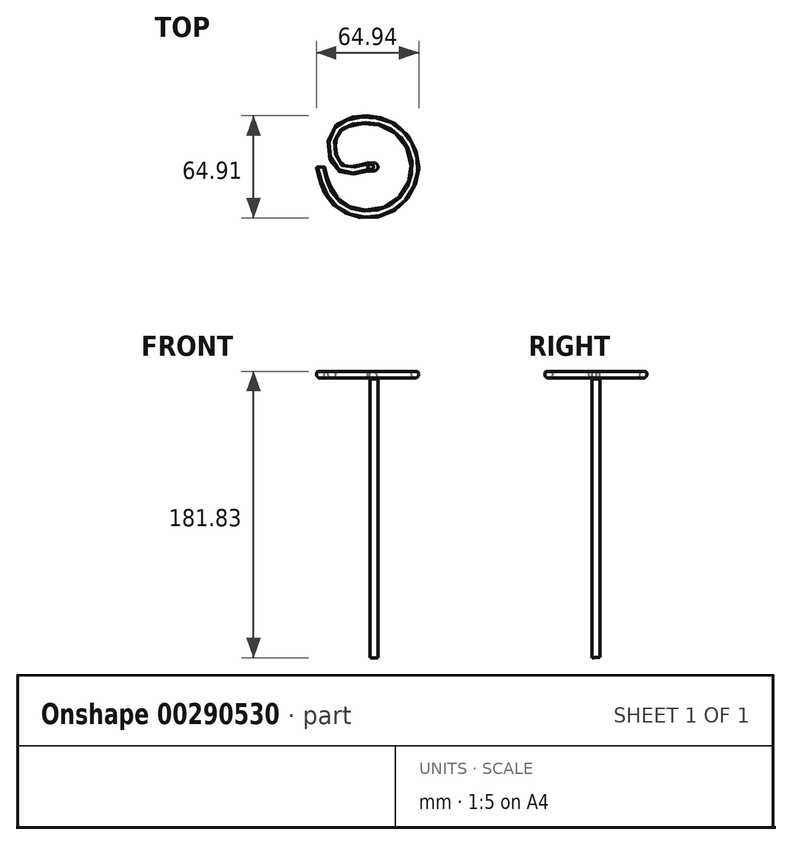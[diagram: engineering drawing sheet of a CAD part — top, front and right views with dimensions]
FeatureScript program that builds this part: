
annotation { "Feature Type Name" : "Feature", "Feature Type Description" : "" }
export const myFeature = defineFeature(function(context is Context, id is Id, definition is map)
    precondition{}
    {
        {
            var Q0;
            Q0=qCreatedBy(makeId("Top.planeOp"),FACE);
            var sketch = newSketch(context, id + "F0", { "sketchPlane" : qUnion([Q0])});
            skArc(sketch, "E0", {"start": v(-21.21, -21.21) * mm, "mid": v(27.72, -11.48) * mm, "end": v(0, 30) * mm});
            skFitSpline(sketch, "E1", {"points": [v(-30, 0) * mm, v(-21.21, -21.21) * mm, v(0, -30) * mm, v(21.21, -21.21) * mm, v(30, 0) * mm, v(21.21, 21.21) * mm, v(0, 30) * mm, v(-21.21, 21.21) * mm, v(-17.95, 0) * mm, v(0, 0) * mm], "startDerivative": vector(49.75, -208.07) * mm, "endDerivative": vector(203.75, 55.38) * mm});
            skSolve(sketch);
        }
        {
            var Q0;
            Q0=qCreatedBy(makeId("Front.planeOp"),FACE);
            var sketch = newSketch(context, id + "F1", { "sketchPlane" : qUnion([Q0])});
            skCircle(sketch, "E2", {"center": v(-30, 0) * mm, "radius": 2.5 * mm});
            skSolve(sketch);
        }
        {
            var Q0;
            Q0=makeQuery(id+"F1.imprint","IMPRINT",FACE,{"disambiguationData":[TD([[makeQuery(id+"F1.imprint","IMPRINT",EDGE,{"derivedFrom":sQuery(id+"F1.wireOp",EDGE,"E2")}),1.0]])]});
            var Q1;
            Q1=sQuery(id+"F0.wireOp",EDGE,"E1");
            sweep(context, id + "F2", {"profiles" : qUnion([Q0]), "path" : qUnion([Q1])});
        }
        {
            var Q0;
            Q0=qCreatedBy(makeId("Front.planeOp"),FACE);
            var sketch = newSketch(context, id + "F3", { "sketchPlane" : qUnion([Q0])});
            skLineSegment(sketch, "E3", {"start": v(0, 0) * mm, "end": v(1, 0) * mm});
            skLineSegment(sketch, "E4", {"start": v(4, -3) * mm, "end": v(4, -180) * mm});
            skPoint(sketch, "E5.visualSharp", {"position": v(4, 0) * mm});
            skArc(sketch, "E5.filletArc", {"start": v(4, -3) * mm, "mid": v(3.12, -0.88) * mm, "end": v(1, 0) * mm});
            skSolve(sketch);
        }
        {
            var Q0;
            Q0=makeQuery(id+"F2.opSweep","CAP_FACE",FACE,{"disambiguationData":[OSD([sQuery(id+"F0.wireOp",VERTEX,"E1.end"),sQuery(id+"F1.wireOp",EDGE,"E2")])],"isStart":false});
            var Q1;
            Q1=sQuery(id+"F3.wireOp",EDGE,"E3");
            var Q2;
            Q2=sQuery(id+"F3.wireOp",EDGE,"E5.filletArc");
            var Q3;
            Q3=sQuery(id+"F3.wireOp",EDGE,"E4");
            sweep(context, id + "F4", {"profiles" : qUnion([Q0]), "path" : qUnion([Q1, Q2, Q3])});
        }
        {
            var Q0;
            Q0=qCreatedBy(makeId("Right.planeOp"),FACE);
            var sketch = newSketch(context, id + "F5", { "sketchPlane" : qUnion([Q0])});
            skLineSegment(sketch, "E6.bottom", {"start": v(-32.1, 1.75) * mm, "end": v(35.71, 1.75) * mm});
            skLineSegment(sketch, "E6.top", {"start": v(-32.1, 11.06) * mm, "end": v(35.71, 11.06) * mm});
            skLineSegment(sketch, "E6.left", {"start": v(-32.1, 1.75) * mm, "end": v(-32.1, 11.06) * mm});
            skLineSegment(sketch, "E6.right", {"start": v(35.71, 1.75) * mm, "end": v(35.71, 11.06) * mm});
            skSolve(sketch);
        }
        {
            var Q0;
            Q0=makeQuery(id+"F5.imprint","IMPRINT",FACE,{"disambiguationData":[TD([[makeQuery(id+"F5.imprint","IMPRINT",EDGE,{"derivedFrom":sQuery(id+"F5.wireOp",EDGE,"E6.bottom")}),1.0]])]});
            extrude(context, id + "F6", {"entities" : qUnion([Q0]), "operationType" : NewBodyOperationType.REMOVE, "oppositeDirection" : true, "depth" : 54.6 * mm});
        }
        {
            var Q0;
            Q0=makeQuery(id+"F5.imprint","IMPRINT",FACE,{"disambiguationData":[TD([[makeQuery(id+"F5.imprint","IMPRINT",EDGE,{"derivedFrom":sQuery(id+"F5.wireOp",EDGE,"E6.bottom")}),1.0]])]});
            extrude(context, id + "F7", {"entities" : qUnion([Q0]), "operationType" : NewBodyOperationType.REMOVE, "depth" : 44.9 * mm});
        }
        {
            var Q0;
            Q0=makeQuery(id+"F5.imprint","IMPRINT",FACE,{"disambiguationData":[TD([[makeQuery(id+"F5.imprint","IMPRINT",EDGE,{"derivedFrom":sQuery(id+"F5.wireOp",EDGE,"E6.bottom")}),1.0]])]});
            extrude(context, id + "F8", {"entities" : qUnion([Q0]), "operationType" : NewBodyOperationType.REMOVE, "depth" : 25 * mm});
        }
    });
